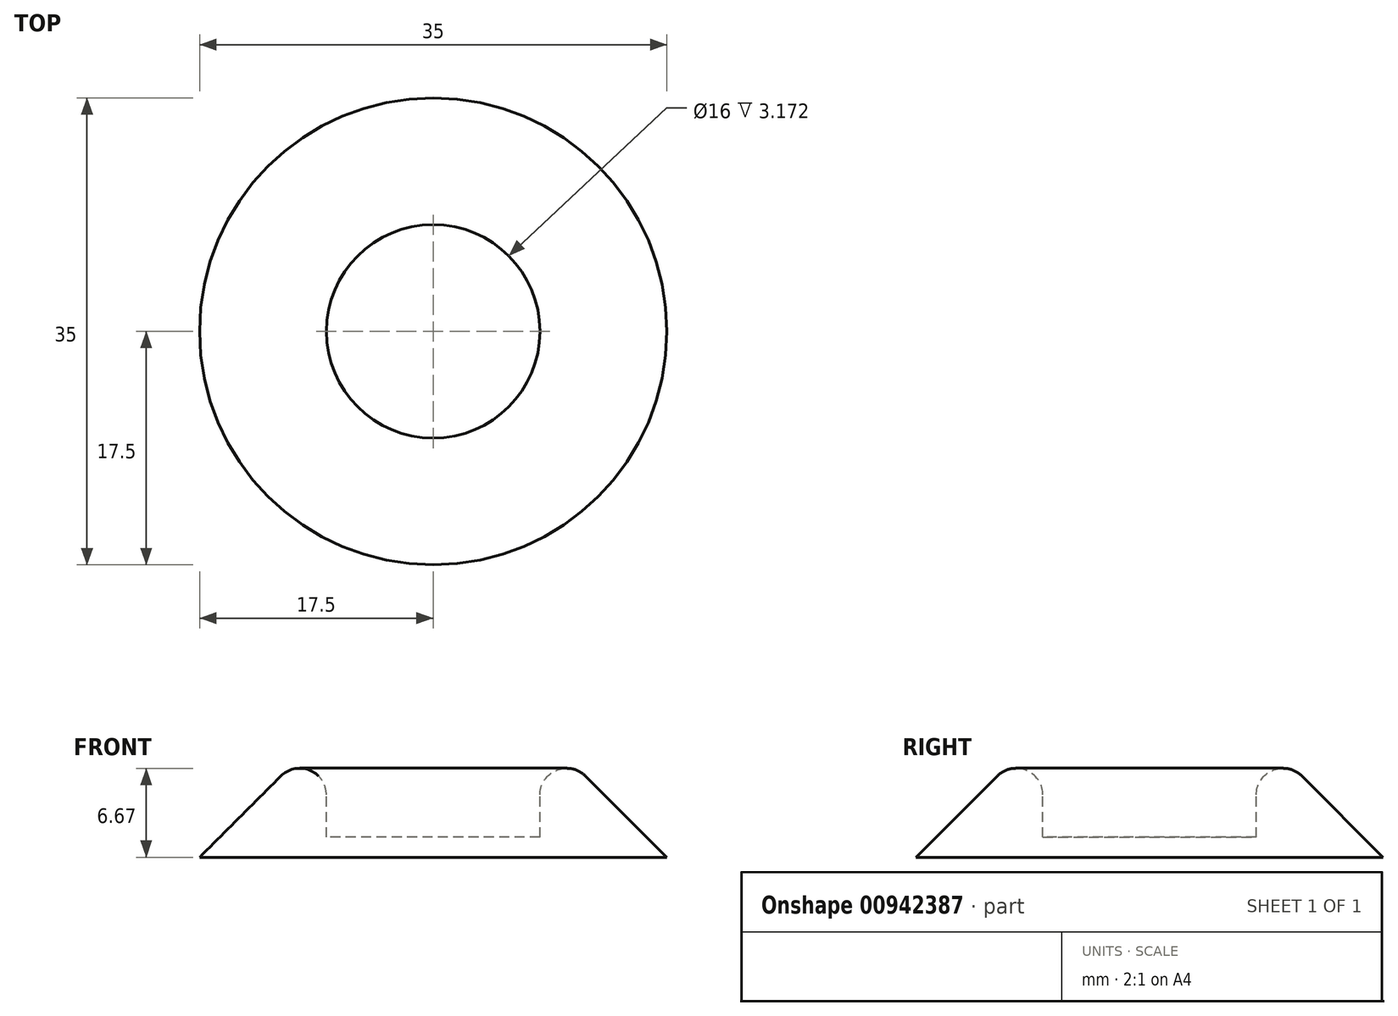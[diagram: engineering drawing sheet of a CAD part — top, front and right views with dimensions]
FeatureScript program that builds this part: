
annotation { "Feature Type Name" : "Feature", "Feature Type Description" : "" }
export const myFeature = defineFeature(function(context is Context, id is Id, definition is map)
    precondition{}
    {
        {
            var Q0;
            Q0=qCreatedBy(makeId("Top.planeOp"),FACE);
            var sketch = newSketch(context, id + "F0", { "sketchPlane" : qUnion([Q0])});
            skCircle(sketch, "E0", {"center": v(0, 0) * mm, "radius": 17.5 * mm});
            skSolve(sketch);
        }
        {
            var Q0;
            Q0=makeQuery(id+"F0.imprint","IMPRINT",FACE,{"disambiguationData":[TD([[makeQuery(id+"F0.imprint","IMPRINT",EDGE,{"derivedFrom":sQuery(id+"F0.wireOp",EDGE,"E0")}),1.0]])]});
            extrude(context, id + "F1", {"entities" : qUnion([Q0]), "depth" : 10 * mm, "offsetDistance" : 25 * mm});
        }
        {
            var Q0;
            Q0=makeQuery(id+"F1.opExtrude","CAP_FACE",FACE,{"disambiguationData":[OSD([sQuery(id+"F0.wireOp",EDGE,"E0")])],"isStart":false});
            var sketch = newSketch(context, id + "F2", { "sketchPlane" : qUnion([Q0])});
            skCircle(sketch, "E1", {"center": v(0, 0) * mm, "radius": 8 * mm});
            skSolve(sketch);
        }
        {
            var Q0;
            Q0=makeQuery(id+"F2.imprint","IMPRINT",FACE,{"disambiguationData":[TD([[makeQuery(id+"F2.imprint","IMPRINT",EDGE,{"derivedFrom":sQuery(id+"F2.wireOp",EDGE,"E1")}),1.0]])]});
            extrude(context, id + "F3", {"entities" : qUnion([Q0]), "operationType" : NewBodyOperationType.REMOVE, "oppositeDirection" : true, "depth" : 8.5 * mm, "offsetDistance" : 25 * mm});
        }
        {
            var Q0;
            Q0=makeQuery(id+"F1.opExtrude","CAP_EDGE",EDGE,{"disambiguationData":[OSD([sQuery(id+"F0.wireOp",EDGE,"E0")])],"isStart":false});
            chamfer(context, id + "F4", {"entities" : qUnion([Q0]), "width" : 10 * mm, "tangentPropagation" : true});
        }
        {
            var Q0;
            Q0=makeQuery(id+"F4.opChamfer","BLEND_EDGE",EDGE,{"blendedFrom":[makeQuery(id+"F1.opExtrude","CAP_EDGE",EDGE,{"disambiguationData":[OSD([sQuery(id+"F0.wireOp",EDGE,"E0")])],"isStart":false}),makeQuery(id+"F3.boolean.opBoolean","COPY",FACE,{"derivedFrom":makeQuery(id+"F3.opExtrude","SWEPT_FACE",FACE,{"disambiguationData":[OSD([sQuery(id+"F2.wireOp",EDGE,"E1")])]})})],"blendedInto":[makeQuery(id+"F3.boolean.opBoolean","COPY",FACE,{"derivedFrom":makeQuery(id+"F3.opExtrude","SWEPT_FACE",FACE,{"disambiguationData":[OSD([sQuery(id+"F2.wireOp",EDGE,"E1")])]})})]});
            fillet(context, id + "F5", {"entities" : qUnion([Q0]), "radius" : 2 * mm, "tangentPropagation" : true, "allowEdgeOverflow" : false});
        }
    });
